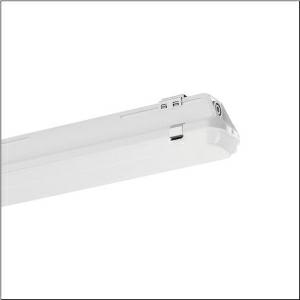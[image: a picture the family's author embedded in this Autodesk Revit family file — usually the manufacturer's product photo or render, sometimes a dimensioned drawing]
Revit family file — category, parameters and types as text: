
# Revit family: monsun_21_51fb107p460c
name_source: partatom
category: Lighting Fixtures
units: mm (PartAtom-declared; Revit-internal decimal feet)

## family parameters
Cut with Voids When Loaded = No
Host = Face
Light Source = No
Part Type = Normal
Room Calculation Point = No
Round Connector Dimension = Use Diameter
Shared = No

## types (1)
- Monsun 21 (1 x LED, 6200 lm, 34.9 W, 4000K)
    Apparent Load = 35 VA
    CIE Flux Codes = 47 77 93 94 100
    Color Rendering = 80
    Color Temperature = 4000K
    Default Elevation = 1800 mm
    Description = Monsun 21, damp-proof luminaire, chain hanger, primary optical cover: enclosure, of PMMA, light emission: direct distribution, primary light characteristic: symmetric, installation type: suspended mounting, surface-mounted, horizontal mounting, vertical mounting, LED, rated luminous flux: 6.200lm, luminous efficacy: 178lm/W, light colour: 840, colour temperature: 4000K, control gear: ON/OFF, with terminal, 3-pole, max. 2.5mm², mains connection: 220..240V, AC, 50/60Hz, rated input power: 35W, housing, of glass-fibre reinforced polyester, uncoated, bright grey, incl. chain hanger, length: 1.590mm, width: 90mm, height: 88mm, clip for enclosure, of stainless steel (V2A), ceiling mounting element, of stainless steel (V2A), chain hanger, of stainless steel (V2A), protection rating (complete): IP66, insulation class (complete): insulation class I (protective earthing), certification: CE, ENEC, VDE, UKCA, protection symbol: D, impact resistance: IK04, permissible operating ambient temperature: -25..+35°C, standard: EN 50419, EN 60598-2-1, corresponds to IFS (International Featured Standards) requirements for safety and quality in the food industry, for indoor or canopied outdoor use, no direct snow, no direct sun, no direct rain, LABS conformity tested according to VDMA 24364:2018-05, contact your sales advisor before using the luminaires in applications with unclear chemical exposure, large temperature fluctuations or condensation-forming humidity, packaging unit: 1 piece
    Height = 89 mm
    Lamp = 1 x LED
    Lamp Light Flux = 6200 lm
    Lamp Power = 34.9 W
    Lamp count = 1
    Length = 1590 mm
    Luminous efficacy = 178 lm/W
    Manufacturer = Siteco
    ModVariant = No
    Model = 51FB107P460C
    Mounting Place = Ceiling
    Mounting Type = Surface mounted
    Number of Poles = 1
    OnlyDefault = Yes
    Power Factor = 1
    Product Name = Monsun 21
    Product group = damp-proof luminaire
    ProductGroupID = 300
    Protection Class = Protection class I
    Protection Degree = IP 66
    RLX_Detail_Level = 1
    RLX_Emergency_Light_Flux = 0 lm
    RLX_Emergency_Type = 0
    RLX_Emergency_Type_DB = No
    RlxData = <blob elided: 88421 chars, md5=a60d198c>
    Socket = socket
    Standby Power = 0 W
    System Light Flux = 6200 lm
    System Power = 35 W
    Type Comments = Product without accessories
    Type Image = l_1319656.jpg
    URL = http://relux.com
    VarID = ---
    Voltage = 0 V
    Weight = 0.00 kg
    Width = 90 mm

## geometry (parser evidence)
native form markers: Blend x4, Sweep x13
no freeform markers — native parametric forms only
